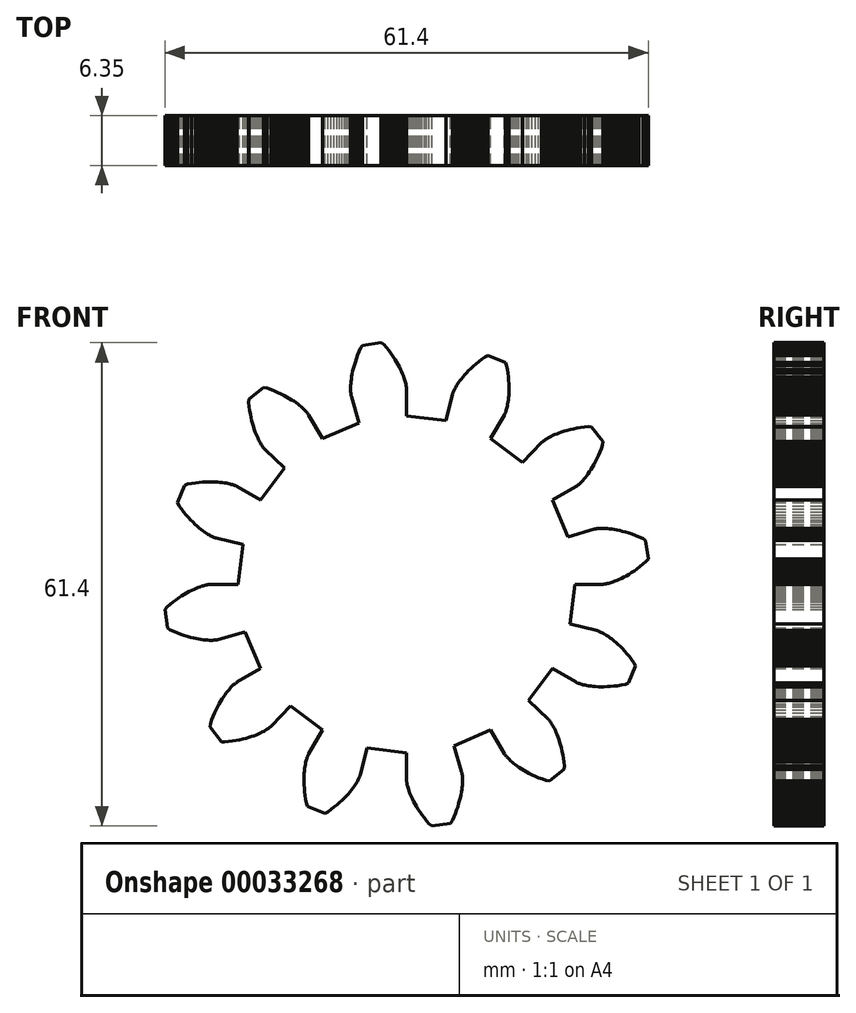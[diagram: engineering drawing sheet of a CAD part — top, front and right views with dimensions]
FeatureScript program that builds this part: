
annotation { "Feature Type Name" : "Feature", "Feature Type Description" : "" }
export const myFeature = defineFeature(function(context is Context, id is Id, definition is map)
    precondition{}
    {
        {
            var Q0;
            Q0=qCreatedBy(makeId("Front.planeOp"),FACE);
            var sketch = newSketch(context, id + "F0", { "sketchPlane" : qUnion([Q0])});
            skLineSegment(sketch, "E0", {"start": v(21.39, 0) * mm, "end": v(24.87, 0) * mm});
            skLineSegment(sketch, "E1", {"start": v(24.87, 0) * mm, "end": v(24.9, 0) * mm});
            skLineSegment(sketch, "E2", {"start": v(24.9, 0) * mm, "end": v(24.93, 0) * mm});
            skLineSegment(sketch, "E3", {"start": v(24.93, 0) * mm, "end": v(25, 0) * mm});
            skLineSegment(sketch, "E4", {"start": v(25, 0) * mm, "end": v(25.08, 0.02) * mm});
            skLineSegment(sketch, "E5", {"start": v(25.08, 0.02) * mm, "end": v(25.2, 0.04) * mm});
            skLineSegment(sketch, "E6", {"start": v(25.2, 0.04) * mm, "end": v(25.32, 0.06) * mm});
            skLineSegment(sketch, "E7", {"start": v(25.32, 0.06) * mm, "end": v(25.46, 0.09) * mm});
            skLineSegment(sketch, "E8", {"start": v(25.46, 0.09) * mm, "end": v(25.63, 0.13) * mm});
            skLineSegment(sketch, "E9", {"start": v(25.63, 0.13) * mm, "end": v(25.81, 0.18) * mm});
            skLineSegment(sketch, "E10", {"start": v(25.81, 0.18) * mm, "end": v(26.02, 0.24) * mm});
            skLineSegment(sketch, "E11", {"start": v(26.02, 0.24) * mm, "end": v(26.24, 0.31) * mm});
            skLineSegment(sketch, "E12", {"start": v(26.24, 0.31) * mm, "end": v(26.48, 0.4) * mm});
            skLineSegment(sketch, "E13", {"start": v(26.48, 0.4) * mm, "end": v(26.73, 0.5) * mm});
            skLineSegment(sketch, "E14", {"start": v(26.73, 0.5) * mm, "end": v(27, 0.62) * mm});
            skLineSegment(sketch, "E15", {"start": v(27, 0.62) * mm, "end": v(27.3, 0.76) * mm});
            skLineSegment(sketch, "E16", {"start": v(27.3, 0.76) * mm, "end": v(27.6, 0.91) * mm});
            skLineSegment(sketch, "E17", {"start": v(27.6, 0.91) * mm, "end": v(27.91, 1.08) * mm});
            skLineSegment(sketch, "E18", {"start": v(27.91, 1.08) * mm, "end": v(28.24, 1.27) * mm});
            skLineSegment(sketch, "E19", {"start": v(28.24, 1.27) * mm, "end": v(28.58, 1.49) * mm});
            skLineSegment(sketch, "E20", {"start": v(28.58, 1.49) * mm, "end": v(28.93, 1.72) * mm});
            skLineSegment(sketch, "E21", {"start": v(28.93, 1.72) * mm, "end": v(29.3, 1.98) * mm});
            skLineSegment(sketch, "E22", {"start": v(29.3, 1.98) * mm, "end": v(29.67, 2.25) * mm});
            skLineSegment(sketch, "E23", {"start": v(29.67, 2.25) * mm, "end": v(30.05, 2.56) * mm});
            skLineSegment(sketch, "E24", {"start": v(30.05, 2.56) * mm, "end": v(30.44, 2.88) * mm});
            skLineSegment(sketch, "E25", {"start": v(30.44, 2.88) * mm, "end": v(30.7, 3.22) * mm});
            skLineSegment(sketch, "E26", {"start": v(30.7, 3.22) * mm, "end": v(30.36, 5.56) * mm});
            skLineSegment(sketch, "E27", {"start": v(30.36, 5.56) * mm, "end": v(30.02, 5.81) * mm});
            skLineSegment(sketch, "E28", {"start": v(30.02, 5.81) * mm, "end": v(29.55, 6.02) * mm});
            skLineSegment(sketch, "E29", {"start": v(29.55, 6.02) * mm, "end": v(29.1, 6.2) * mm});
            skLineSegment(sketch, "E30", {"start": v(29.1, 6.2) * mm, "end": v(28.66, 6.36) * mm});
            skLineSegment(sketch, "E31", {"start": v(28.66, 6.36) * mm, "end": v(28.25, 6.5) * mm});
            skLineSegment(sketch, "E32", {"start": v(28.25, 6.5) * mm, "end": v(27.84, 6.63) * mm});
            skLineSegment(sketch, "E33", {"start": v(27.84, 6.63) * mm, "end": v(27.45, 6.74) * mm});
            skLineSegment(sketch, "E34", {"start": v(27.45, 6.74) * mm, "end": v(27.08, 6.83) * mm});
            skLineSegment(sketch, "E35", {"start": v(27.08, 6.83) * mm, "end": v(26.73, 6.9) * mm});
            skLineSegment(sketch, "E36", {"start": v(26.73, 6.9) * mm, "end": v(26.4, 6.97) * mm});
            skLineSegment(sketch, "E37", {"start": v(26.4, 6.97) * mm, "end": v(26.08, 7.02) * mm});
            skLineSegment(sketch, "E38", {"start": v(26.08, 7.02) * mm, "end": v(25.8, 7.05) * mm});
            skLineSegment(sketch, "E39", {"start": v(25.8, 7.05) * mm, "end": v(25.52, 7.08) * mm});
            skLineSegment(sketch, "E40", {"start": v(25.52, 7.08) * mm, "end": v(25.26, 7.1) * mm});
            skLineSegment(sketch, "E41", {"start": v(25.26, 7.1) * mm, "end": v(25.03, 7.1) * mm});
            skLineSegment(sketch, "E42", {"start": v(25.03, 7.1) * mm, "end": v(24.82, 7.1) * mm});
            skLineSegment(sketch, "E43", {"start": v(24.82, 7.1) * mm, "end": v(24.63, 7.1) * mm});
            skLineSegment(sketch, "E44", {"start": v(24.63, 7.1) * mm, "end": v(24.45, 7.1) * mm});
            skLineSegment(sketch, "E45", {"start": v(24.45, 7.1) * mm, "end": v(24.3, 7.08) * mm});
            skLineSegment(sketch, "E46", {"start": v(24.3, 7.08) * mm, "end": v(24.18, 7.07) * mm});
            skLineSegment(sketch, "E47", {"start": v(24.18, 7.07) * mm, "end": v(24.07, 7.05) * mm});
            skLineSegment(sketch, "E48", {"start": v(24.07, 7.05) * mm, "end": v(23.99, 7.04) * mm});
            skLineSegment(sketch, "E49", {"start": v(23.99, 7.04) * mm, "end": v(23.92, 7.03) * mm});
            skLineSegment(sketch, "E50", {"start": v(23.92, 7.03) * mm, "end": v(23.88, 7.02) * mm});
            skLineSegment(sketch, "E51", {"start": v(23.88, 7.02) * mm, "end": v(23.86, 7.01) * mm});
            skLineSegment(sketch, "E52", {"start": v(23.86, 7.01) * mm, "end": v(20.52, 6.03) * mm});
            skLineSegment(sketch, "E53", {"start": v(20.52, 6.03) * mm, "end": v(18.52, 10.7) * mm});
            skLineSegment(sketch, "E54", {"start": v(18.52, 10.7) * mm, "end": v(21.53, 12.43) * mm});
            skLineSegment(sketch, "E55", {"start": v(21.53, 12.43) * mm, "end": v(21.56, 12.45) * mm});
            skLineSegment(sketch, "E56", {"start": v(21.56, 12.45) * mm, "end": v(21.64, 12.5) * mm});
            skLineSegment(sketch, "E57", {"start": v(21.64, 12.5) * mm, "end": v(21.71, 12.56) * mm});
            skLineSegment(sketch, "E58", {"start": v(21.71, 12.56) * mm, "end": v(21.8, 12.63) * mm});
            skLineSegment(sketch, "E59", {"start": v(21.8, 12.63) * mm, "end": v(21.9, 12.7) * mm});
            skLineSegment(sketch, "E60", {"start": v(21.9, 12.7) * mm, "end": v(22, 12.8) * mm});
            skLineSegment(sketch, "E61", {"start": v(22, 12.8) * mm, "end": v(22.13, 12.93) * mm});
            skLineSegment(sketch, "E62", {"start": v(22.13, 12.93) * mm, "end": v(22.26, 13.06) * mm});
            skLineSegment(sketch, "E63", {"start": v(22.26, 13.06) * mm, "end": v(22.41, 13.22) * mm});
            skLineSegment(sketch, "E64", {"start": v(22.41, 13.22) * mm, "end": v(22.57, 13.4) * mm});
            skLineSegment(sketch, "E65", {"start": v(22.57, 13.4) * mm, "end": v(22.73, 13.59) * mm});
            skLineSegment(sketch, "E66", {"start": v(22.73, 13.59) * mm, "end": v(22.9, 13.8) * mm});
            skLineSegment(sketch, "E67", {"start": v(22.9, 13.8) * mm, "end": v(23.08, 14.04) * mm});
            skLineSegment(sketch, "E68", {"start": v(23.08, 14.04) * mm, "end": v(23.26, 14.3) * mm});
            skLineSegment(sketch, "E69", {"start": v(23.26, 14.3) * mm, "end": v(23.44, 14.59) * mm});
            skLineSegment(sketch, "E70", {"start": v(23.44, 14.59) * mm, "end": v(23.63, 14.9) * mm});
            skLineSegment(sketch, "E71", {"start": v(23.63, 14.9) * mm, "end": v(23.82, 15.22) * mm});
            skLineSegment(sketch, "E72", {"start": v(23.82, 15.22) * mm, "end": v(24, 15.58) * mm});
            skLineSegment(sketch, "E73", {"start": v(24, 15.58) * mm, "end": v(24.2, 15.96) * mm});
            skLineSegment(sketch, "E74", {"start": v(24.2, 15.96) * mm, "end": v(24.38, 16.36) * mm});
            skLineSegment(sketch, "E75", {"start": v(24.38, 16.36) * mm, "end": v(24.57, 16.79) * mm});
            skLineSegment(sketch, "E76", {"start": v(24.57, 16.79) * mm, "end": v(24.74, 17.24) * mm});
            skLineSegment(sketch, "E77", {"start": v(24.74, 17.24) * mm, "end": v(24.92, 17.72) * mm});
            skLineSegment(sketch, "E78", {"start": v(24.92, 17.72) * mm, "end": v(24.98, 18.14) * mm});
            skLineSegment(sketch, "E79", {"start": v(24.98, 18.14) * mm, "end": v(23.51, 20) * mm});
            skLineSegment(sketch, "E80", {"start": v(23.51, 20) * mm, "end": v(23.09, 20.04) * mm});
            skLineSegment(sketch, "E81", {"start": v(23.09, 20.04) * mm, "end": v(22.58, 19.99) * mm});
            skLineSegment(sketch, "E82", {"start": v(22.58, 19.99) * mm, "end": v(22.1, 19.92) * mm});
            skLineSegment(sketch, "E83", {"start": v(22.1, 19.92) * mm, "end": v(21.64, 19.84) * mm});
            skLineSegment(sketch, "E84", {"start": v(21.64, 19.84) * mm, "end": v(21.2, 19.76) * mm});
            skLineSegment(sketch, "E85", {"start": v(21.2, 19.76) * mm, "end": v(20.8, 19.66) * mm});
            skLineSegment(sketch, "E86", {"start": v(20.8, 19.66) * mm, "end": v(20.4, 19.56) * mm});
            skLineSegment(sketch, "E87", {"start": v(20.4, 19.56) * mm, "end": v(20.04, 19.46) * mm});
            skLineSegment(sketch, "E88", {"start": v(20.04, 19.46) * mm, "end": v(19.7, 19.35) * mm});
            skLineSegment(sketch, "E89", {"start": v(19.7, 19.35) * mm, "end": v(19.38, 19.23) * mm});
            skLineSegment(sketch, "E90", {"start": v(19.38, 19.23) * mm, "end": v(19.08, 19.12) * mm});
            skLineSegment(sketch, "E91", {"start": v(19.08, 19.12) * mm, "end": v(18.81, 19) * mm});
            skLineSegment(sketch, "E92", {"start": v(18.81, 19) * mm, "end": v(18.56, 18.89) * mm});
            skLineSegment(sketch, "E93", {"start": v(18.56, 18.89) * mm, "end": v(18.33, 18.78) * mm});
            skLineSegment(sketch, "E94", {"start": v(18.33, 18.78) * mm, "end": v(18.12, 18.67) * mm});
            skLineSegment(sketch, "E95", {"start": v(18.12, 18.67) * mm, "end": v(17.94, 18.56) * mm});
            skLineSegment(sketch, "E96", {"start": v(17.94, 18.56) * mm, "end": v(17.78, 18.46) * mm});
            skLineSegment(sketch, "E97", {"start": v(17.78, 18.46) * mm, "end": v(17.63, 18.37) * mm});
            skLineSegment(sketch, "E98", {"start": v(17.63, 18.37) * mm, "end": v(17.5, 18.29) * mm});
            skLineSegment(sketch, "E99", {"start": v(17.5, 18.29) * mm, "end": v(17.4, 18.2) * mm});
            skLineSegment(sketch, "E100", {"start": v(17.4, 18.2) * mm, "end": v(17.32, 18.14) * mm});
            skLineSegment(sketch, "E101", {"start": v(17.32, 18.14) * mm, "end": v(17.25, 18.09) * mm});
            skLineSegment(sketch, "E102", {"start": v(17.25, 18.09) * mm, "end": v(17.2, 18.05) * mm});
            skLineSegment(sketch, "E103", {"start": v(17.2, 18.05) * mm, "end": v(17.17, 18.02) * mm});
            skLineSegment(sketch, "E104", {"start": v(17.17, 18.02) * mm, "end": v(17.16, 18) * mm});
            skLineSegment(sketch, "E105", {"start": v(17.16, 18) * mm, "end": v(14.76, 15.48) * mm});
            skLineSegment(sketch, "E106", {"start": v(14.76, 15.48) * mm, "end": v(10.7, 18.52) * mm});
            skLineSegment(sketch, "E107", {"start": v(10.7, 18.52) * mm, "end": v(12.43, 21.53) * mm});
            skLineSegment(sketch, "E108", {"start": v(12.43, 21.53) * mm, "end": v(12.44, 21.56) * mm});
            skLineSegment(sketch, "E109", {"start": v(12.44, 21.56) * mm, "end": v(12.46, 21.6) * mm});
            skLineSegment(sketch, "E110", {"start": v(12.46, 21.6) * mm, "end": v(12.5, 21.65) * mm});
            skLineSegment(sketch, "E111", {"start": v(12.5, 21.65) * mm, "end": v(12.53, 21.73) * mm});
            skLineSegment(sketch, "E112", {"start": v(12.53, 21.73) * mm, "end": v(12.56, 21.83) * mm});
            skLineSegment(sketch, "E113", {"start": v(12.56, 21.83) * mm, "end": v(12.6, 21.95) * mm});
            skLineSegment(sketch, "E114", {"start": v(12.6, 21.95) * mm, "end": v(12.65, 22.1) * mm});
            skLineSegment(sketch, "E115", {"start": v(12.65, 22.1) * mm, "end": v(12.7, 22.26) * mm});
            skLineSegment(sketch, "E116", {"start": v(12.7, 22.26) * mm, "end": v(12.75, 22.44) * mm});
            skLineSegment(sketch, "E117", {"start": v(12.75, 22.44) * mm, "end": v(12.8, 22.65) * mm});
            skLineSegment(sketch, "E118", {"start": v(12.8, 22.65) * mm, "end": v(12.85, 22.88) * mm});
            skLineSegment(sketch, "E119", {"start": v(12.85, 22.88) * mm, "end": v(12.9, 23.13) * mm});
            skLineSegment(sketch, "E120", {"start": v(12.9, 23.13) * mm, "end": v(12.93, 23.4) * mm});
            skLineSegment(sketch, "E121", {"start": v(12.93, 23.4) * mm, "end": v(12.96, 23.7) * mm});
            skLineSegment(sketch, "E122", {"start": v(12.96, 23.7) * mm, "end": v(12.99, 24.02) * mm});
            skLineSegment(sketch, "E123", {"start": v(12.99, 24.02) * mm, "end": v(13, 24.35) * mm});
            skLineSegment(sketch, "E124", {"start": v(13, 24.35) * mm, "end": v(13.02, 24.71) * mm});
            skLineSegment(sketch, "E125", {"start": v(13.02, 24.71) * mm, "end": v(13.02, 25.1) * mm});
            skLineSegment(sketch, "E126", {"start": v(13.02, 25.1) * mm, "end": v(13, 25.5) * mm});
            skLineSegment(sketch, "E127", {"start": v(13, 25.5) * mm, "end": v(12.98, 25.92) * mm});
            skLineSegment(sketch, "E128", {"start": v(12.98, 25.92) * mm, "end": v(12.94, 26.36) * mm});
            skLineSegment(sketch, "E129", {"start": v(12.94, 26.36) * mm, "end": v(12.88, 26.82) * mm});
            skLineSegment(sketch, "E130", {"start": v(12.88, 26.82) * mm, "end": v(12.81, 27.3) * mm});
            skLineSegment(sketch, "E131", {"start": v(12.81, 27.3) * mm, "end": v(12.72, 27.8) * mm});
            skLineSegment(sketch, "E132", {"start": v(12.72, 27.8) * mm, "end": v(12.56, 28.2) * mm});
            skLineSegment(sketch, "E133", {"start": v(12.56, 28.2) * mm, "end": v(10.36, 29.08) * mm});
            skLineSegment(sketch, "E134", {"start": v(10.36, 29.08) * mm, "end": v(9.97, 28.9) * mm});
            skLineSegment(sketch, "E135", {"start": v(9.97, 28.9) * mm, "end": v(9.56, 28.6) * mm});
            skLineSegment(sketch, "E136", {"start": v(9.56, 28.6) * mm, "end": v(9.18, 28.3) * mm});
            skLineSegment(sketch, "E137", {"start": v(9.18, 28.3) * mm, "end": v(8.82, 28) * mm});
            skLineSegment(sketch, "E138", {"start": v(8.82, 28) * mm, "end": v(8.49, 27.71) * mm});
            skLineSegment(sketch, "E139", {"start": v(8.49, 27.71) * mm, "end": v(8.18, 27.43) * mm});
            skLineSegment(sketch, "E140", {"start": v(8.18, 27.43) * mm, "end": v(7.9, 27.14) * mm});
            skLineSegment(sketch, "E141", {"start": v(7.9, 27.14) * mm, "end": v(7.63, 26.87) * mm});
            skLineSegment(sketch, "E142", {"start": v(7.63, 26.87) * mm, "end": v(7.39, 26.6) * mm});
            skLineSegment(sketch, "E143", {"start": v(7.39, 26.6) * mm, "end": v(7.17, 26.35) * mm});
            skLineSegment(sketch, "E144", {"start": v(7.17, 26.35) * mm, "end": v(6.97, 26.1) * mm});
            skLineSegment(sketch, "E145", {"start": v(6.97, 26.1) * mm, "end": v(6.79, 25.86) * mm});
            skLineSegment(sketch, "E146", {"start": v(6.79, 25.86) * mm, "end": v(6.63, 25.64) * mm});
            skLineSegment(sketch, "E147", {"start": v(6.63, 25.64) * mm, "end": v(6.49, 25.43) * mm});
            skLineSegment(sketch, "E148", {"start": v(6.49, 25.43) * mm, "end": v(6.36, 25.23) * mm});
            skLineSegment(sketch, "E149", {"start": v(6.36, 25.23) * mm, "end": v(6.25, 25.04) * mm});
            skLineSegment(sketch, "E150", {"start": v(6.25, 25.04) * mm, "end": v(6.16, 24.88) * mm});
            skLineSegment(sketch, "E151", {"start": v(6.16, 24.88) * mm, "end": v(6.09, 24.72) * mm});
            skLineSegment(sketch, "E152", {"start": v(6.09, 24.72) * mm, "end": v(6.02, 24.6) * mm});
            skLineSegment(sketch, "E153", {"start": v(6.02, 24.6) * mm, "end": v(5.97, 24.47) * mm});
            skLineSegment(sketch, "E154", {"start": v(5.97, 24.47) * mm, "end": v(5.93, 24.37) * mm});
            skLineSegment(sketch, "E155", {"start": v(5.93, 24.37) * mm, "end": v(5.9, 24.3) * mm});
            skLineSegment(sketch, "E156", {"start": v(5.9, 24.3) * mm, "end": v(5.88, 24.23) * mm});
            skLineSegment(sketch, "E157", {"start": v(5.88, 24.23) * mm, "end": v(5.86, 24.19) * mm});
            skLineSegment(sketch, "E158", {"start": v(5.86, 24.19) * mm, "end": v(5.86, 24.17) * mm});
            skLineSegment(sketch, "E159", {"start": v(5.86, 24.17) * mm, "end": v(5.04, 20.79) * mm});
            skLineSegment(sketch, "E160", {"start": v(5.04, 20.79) * mm, "end": v(0, 21.39) * mm});
            skLineSegment(sketch, "E161", {"start": v(0, 21.39) * mm, "end": v(0, 24.87) * mm});
            skLineSegment(sketch, "E162", {"start": v(0, 24.87) * mm, "end": v(0, 24.9) * mm});
            skLineSegment(sketch, "E163", {"start": v(0, 24.9) * mm, "end": v(0, 24.93) * mm});
            skLineSegment(sketch, "E164", {"start": v(0, 24.93) * mm, "end": v(0, 25) * mm});
            skLineSegment(sketch, "E165", {"start": v(0, 25) * mm, "end": v(-0.02, 25.08) * mm});
            skLineSegment(sketch, "E166", {"start": v(-0.02, 25.08) * mm, "end": v(-0.04, 25.2) * mm});
            skLineSegment(sketch, "E167", {"start": v(-0.04, 25.2) * mm, "end": v(-0.06, 25.32) * mm});
            skLineSegment(sketch, "E168", {"start": v(-0.06, 25.32) * mm, "end": v(-0.09, 25.46) * mm});
            skLineSegment(sketch, "E169", {"start": v(-0.09, 25.46) * mm, "end": v(-0.13, 25.63) * mm});
            skLineSegment(sketch, "E170", {"start": v(-0.13, 25.63) * mm, "end": v(-0.18, 25.81) * mm});
            skLineSegment(sketch, "E171", {"start": v(-0.18, 25.81) * mm, "end": v(-0.24, 26.02) * mm});
            skLineSegment(sketch, "E172", {"start": v(-0.24, 26.02) * mm, "end": v(-0.31, 26.24) * mm});
            skLineSegment(sketch, "E173", {"start": v(-0.31, 26.24) * mm, "end": v(-0.4, 26.48) * mm});
            skLineSegment(sketch, "E174", {"start": v(-0.4, 26.48) * mm, "end": v(-0.5, 26.73) * mm});
            skLineSegment(sketch, "E175", {"start": v(-0.5, 26.73) * mm, "end": v(-0.62, 27) * mm});
            skLineSegment(sketch, "E176", {"start": v(-0.62, 27) * mm, "end": v(-0.76, 27.3) * mm});
            skLineSegment(sketch, "E177", {"start": v(-0.76, 27.3) * mm, "end": v(-0.91, 27.6) * mm});
            skLineSegment(sketch, "E178", {"start": v(-0.91, 27.6) * mm, "end": v(-1.08, 27.91) * mm});
            skLineSegment(sketch, "E179", {"start": v(-1.08, 27.91) * mm, "end": v(-1.27, 28.24) * mm});
            skLineSegment(sketch, "E180", {"start": v(-1.27, 28.24) * mm, "end": v(-1.49, 28.58) * mm});
            skLineSegment(sketch, "E181", {"start": v(-1.49, 28.58) * mm, "end": v(-1.72, 28.93) * mm});
            skLineSegment(sketch, "E182", {"start": v(-1.72, 28.93) * mm, "end": v(-1.98, 29.3) * mm});
            skLineSegment(sketch, "E183", {"start": v(-1.98, 29.3) * mm, "end": v(-2.25, 29.67) * mm});
            skLineSegment(sketch, "E184", {"start": v(-2.25, 29.67) * mm, "end": v(-2.56, 30.05) * mm});
            skLineSegment(sketch, "E185", {"start": v(-2.56, 30.05) * mm, "end": v(-2.88, 30.44) * mm});
            skLineSegment(sketch, "E186", {"start": v(-2.88, 30.44) * mm, "end": v(-3.22, 30.7) * mm});
            skLineSegment(sketch, "E187", {"start": v(-3.22, 30.7) * mm, "end": v(-5.56, 30.36) * mm});
            skLineSegment(sketch, "E188", {"start": v(-5.56, 30.36) * mm, "end": v(-5.81, 30.02) * mm});
            skLineSegment(sketch, "E189", {"start": v(-5.81, 30.02) * mm, "end": v(-6.02, 29.55) * mm});
            skLineSegment(sketch, "E190", {"start": v(-6.02, 29.55) * mm, "end": v(-6.2, 29.1) * mm});
            skLineSegment(sketch, "E191", {"start": v(-6.2, 29.1) * mm, "end": v(-6.36, 28.66) * mm});
            skLineSegment(sketch, "E192", {"start": v(-6.36, 28.66) * mm, "end": v(-6.5, 28.25) * mm});
            skLineSegment(sketch, "E193", {"start": v(-6.5, 28.25) * mm, "end": v(-6.63, 27.84) * mm});
            skLineSegment(sketch, "E194", {"start": v(-6.63, 27.84) * mm, "end": v(-6.74, 27.45) * mm});
            skLineSegment(sketch, "E195", {"start": v(-6.74, 27.45) * mm, "end": v(-6.83, 27.08) * mm});
            skLineSegment(sketch, "E196", {"start": v(-6.83, 27.08) * mm, "end": v(-6.9, 26.73) * mm});
            skLineSegment(sketch, "E197", {"start": v(-6.9, 26.73) * mm, "end": v(-6.97, 26.4) * mm});
            skLineSegment(sketch, "E198", {"start": v(-6.97, 26.4) * mm, "end": v(-7.02, 26.08) * mm});
            skLineSegment(sketch, "E199", {"start": v(-7.02, 26.08) * mm, "end": v(-7.05, 25.8) * mm});
            skLineSegment(sketch, "E200", {"start": v(-7.05, 25.8) * mm, "end": v(-7.08, 25.52) * mm});
            skLineSegment(sketch, "E201", {"start": v(-7.08, 25.52) * mm, "end": v(-7.1, 25.26) * mm});
            skLineSegment(sketch, "E202", {"start": v(-7.1, 25.26) * mm, "end": v(-7.1, 25.03) * mm});
            skLineSegment(sketch, "E203", {"start": v(-7.1, 25.03) * mm, "end": v(-7.1, 24.82) * mm});
            skLineSegment(sketch, "E204", {"start": v(-7.1, 24.82) * mm, "end": v(-7.1, 24.63) * mm});
            skLineSegment(sketch, "E205", {"start": v(-7.1, 24.63) * mm, "end": v(-7.1, 24.45) * mm});
            skLineSegment(sketch, "E206", {"start": v(-7.1, 24.45) * mm, "end": v(-7.08, 24.3) * mm});
            skLineSegment(sketch, "E207", {"start": v(-7.08, 24.3) * mm, "end": v(-7.07, 24.18) * mm});
            skLineSegment(sketch, "E208", {"start": v(-7.07, 24.18) * mm, "end": v(-7.05, 24.07) * mm});
            skLineSegment(sketch, "E209", {"start": v(-7.05, 24.07) * mm, "end": v(-7.04, 23.99) * mm});
            skLineSegment(sketch, "E210", {"start": v(-7.04, 23.99) * mm, "end": v(-7.03, 23.92) * mm});
            skLineSegment(sketch, "E211", {"start": v(-7.03, 23.92) * mm, "end": v(-7.02, 23.88) * mm});
            skLineSegment(sketch, "E212", {"start": v(-7.02, 23.88) * mm, "end": v(-7, 23.86) * mm});
            skLineSegment(sketch, "E213", {"start": v(-7, 23.86) * mm, "end": v(-6.03, 20.52) * mm});
            skLineSegment(sketch, "E214", {"start": v(-6.03, 20.52) * mm, "end": v(-10.7, 18.52) * mm});
            skLineSegment(sketch, "E215", {"start": v(-10.7, 18.52) * mm, "end": v(-12.43, 21.53) * mm});
            skLineSegment(sketch, "E216", {"start": v(-12.43, 21.53) * mm, "end": v(-12.44, 21.56) * mm});
            skLineSegment(sketch, "E217", {"start": v(-12.44, 21.56) * mm, "end": v(-12.5, 21.64) * mm});
            skLineSegment(sketch, "E218", {"start": v(-12.5, 21.64) * mm, "end": v(-12.56, 21.71) * mm});
            skLineSegment(sketch, "E219", {"start": v(-12.56, 21.71) * mm, "end": v(-12.63, 21.8) * mm});
            skLineSegment(sketch, "E220", {"start": v(-12.63, 21.8) * mm, "end": v(-12.7, 21.9) * mm});
            skLineSegment(sketch, "E221", {"start": v(-12.7, 21.9) * mm, "end": v(-12.8, 22) * mm});
            skLineSegment(sketch, "E222", {"start": v(-12.8, 22) * mm, "end": v(-12.93, 22.13) * mm});
            skLineSegment(sketch, "E223", {"start": v(-12.93, 22.13) * mm, "end": v(-13.06, 22.26) * mm});
            skLineSegment(sketch, "E224", {"start": v(-13.06, 22.26) * mm, "end": v(-13.22, 22.41) * mm});
            skLineSegment(sketch, "E225", {"start": v(-13.22, 22.41) * mm, "end": v(-13.4, 22.57) * mm});
            skLineSegment(sketch, "E226", {"start": v(-13.4, 22.57) * mm, "end": v(-13.59, 22.73) * mm});
            skLineSegment(sketch, "E227", {"start": v(-13.59, 22.73) * mm, "end": v(-13.8, 22.9) * mm});
            skLineSegment(sketch, "E228", {"start": v(-13.8, 22.9) * mm, "end": v(-14.04, 23.08) * mm});
            skLineSegment(sketch, "E229", {"start": v(-14.04, 23.08) * mm, "end": v(-14.3, 23.26) * mm});
            skLineSegment(sketch, "E230", {"start": v(-14.3, 23.26) * mm, "end": v(-14.59, 23.44) * mm});
            skLineSegment(sketch, "E231", {"start": v(-14.59, 23.44) * mm, "end": v(-14.9, 23.63) * mm});
            skLineSegment(sketch, "E232", {"start": v(-14.9, 23.63) * mm, "end": v(-15.22, 23.82) * mm});
            skLineSegment(sketch, "E233", {"start": v(-15.22, 23.82) * mm, "end": v(-15.58, 24) * mm});
            skLineSegment(sketch, "E234", {"start": v(-15.58, 24) * mm, "end": v(-15.96, 24.2) * mm});
            skLineSegment(sketch, "E235", {"start": v(-15.96, 24.2) * mm, "end": v(-16.36, 24.38) * mm});
            skLineSegment(sketch, "E236", {"start": v(-16.36, 24.38) * mm, "end": v(-16.79, 24.57) * mm});
            skLineSegment(sketch, "E237", {"start": v(-16.79, 24.57) * mm, "end": v(-17.24, 24.74) * mm});
            skLineSegment(sketch, "E238", {"start": v(-17.24, 24.74) * mm, "end": v(-17.72, 24.92) * mm});
            skLineSegment(sketch, "E239", {"start": v(-17.72, 24.92) * mm, "end": v(-18.14, 24.98) * mm});
            skLineSegment(sketch, "E240", {"start": v(-18.14, 24.98) * mm, "end": v(-20, 23.51) * mm});
            skLineSegment(sketch, "E241", {"start": v(-20, 23.51) * mm, "end": v(-20.04, 23.09) * mm});
            skLineSegment(sketch, "E242", {"start": v(-20.04, 23.09) * mm, "end": v(-19.99, 22.58) * mm});
            skLineSegment(sketch, "E243", {"start": v(-19.99, 22.58) * mm, "end": v(-19.92, 22.1) * mm});
            skLineSegment(sketch, "E244", {"start": v(-19.92, 22.1) * mm, "end": v(-19.84, 21.64) * mm});
            skLineSegment(sketch, "E245", {"start": v(-19.84, 21.64) * mm, "end": v(-19.76, 21.2) * mm});
            skLineSegment(sketch, "E246", {"start": v(-19.76, 21.2) * mm, "end": v(-19.66, 20.8) * mm});
            skLineSegment(sketch, "E247", {"start": v(-19.66, 20.8) * mm, "end": v(-19.56, 20.4) * mm});
            skLineSegment(sketch, "E248", {"start": v(-19.56, 20.4) * mm, "end": v(-19.46, 20.04) * mm});
            skLineSegment(sketch, "E249", {"start": v(-19.46, 20.04) * mm, "end": v(-19.35, 19.7) * mm});
            skLineSegment(sketch, "E250", {"start": v(-19.35, 19.7) * mm, "end": v(-19.23, 19.38) * mm});
            skLineSegment(sketch, "E251", {"start": v(-19.23, 19.38) * mm, "end": v(-19.12, 19.08) * mm});
            skLineSegment(sketch, "E252", {"start": v(-19.12, 19.08) * mm, "end": v(-19, 18.81) * mm});
            skLineSegment(sketch, "E253", {"start": v(-19, 18.81) * mm, "end": v(-18.89, 18.56) * mm});
            skLineSegment(sketch, "E254", {"start": v(-18.89, 18.56) * mm, "end": v(-18.78, 18.33) * mm});
            skLineSegment(sketch, "E255", {"start": v(-18.78, 18.33) * mm, "end": v(-18.67, 18.12) * mm});
            skLineSegment(sketch, "E256", {"start": v(-18.67, 18.12) * mm, "end": v(-18.56, 17.94) * mm});
            skLineSegment(sketch, "E257", {"start": v(-18.56, 17.94) * mm, "end": v(-18.46, 17.78) * mm});
            skLineSegment(sketch, "E258", {"start": v(-18.46, 17.78) * mm, "end": v(-18.37, 17.63) * mm});
            skLineSegment(sketch, "E259", {"start": v(-18.37, 17.63) * mm, "end": v(-18.29, 17.5) * mm});
            skLineSegment(sketch, "E260", {"start": v(-18.29, 17.5) * mm, "end": v(-18.2, 17.4) * mm});
            skLineSegment(sketch, "E261", {"start": v(-18.2, 17.4) * mm, "end": v(-18.14, 17.32) * mm});
            skLineSegment(sketch, "E262", {"start": v(-18.14, 17.32) * mm, "end": v(-18.09, 17.25) * mm});
            skLineSegment(sketch, "E263", {"start": v(-18.09, 17.25) * mm, "end": v(-18.05, 17.2) * mm});
            skLineSegment(sketch, "E264", {"start": v(-18.05, 17.2) * mm, "end": v(-18.02, 17.17) * mm});
            skLineSegment(sketch, "E265", {"start": v(-18.02, 17.17) * mm, "end": v(-18, 17.16) * mm});
            skLineSegment(sketch, "E266", {"start": v(-18, 17.16) * mm, "end": v(-15.48, 14.76) * mm});
            skLineSegment(sketch, "E267", {"start": v(-15.48, 14.76) * mm, "end": v(-18.52, 10.7) * mm});
            skLineSegment(sketch, "E268", {"start": v(-18.52, 10.7) * mm, "end": v(-21.53, 12.43) * mm});
            skLineSegment(sketch, "E269", {"start": v(-21.53, 12.43) * mm, "end": v(-21.56, 12.44) * mm});
            skLineSegment(sketch, "E270", {"start": v(-21.56, 12.44) * mm, "end": v(-21.6, 12.46) * mm});
            skLineSegment(sketch, "E271", {"start": v(-21.6, 12.46) * mm, "end": v(-21.65, 12.5) * mm});
            skLineSegment(sketch, "E272", {"start": v(-21.65, 12.5) * mm, "end": v(-21.73, 12.53) * mm});
            skLineSegment(sketch, "E273", {"start": v(-21.73, 12.53) * mm, "end": v(-21.83, 12.56) * mm});
            skLineSegment(sketch, "E274", {"start": v(-21.83, 12.56) * mm, "end": v(-21.95, 12.6) * mm});
            skLineSegment(sketch, "E275", {"start": v(-21.95, 12.6) * mm, "end": v(-22.1, 12.65) * mm});
            skLineSegment(sketch, "E276", {"start": v(-22.1, 12.65) * mm, "end": v(-22.26, 12.7) * mm});
            skLineSegment(sketch, "E277", {"start": v(-22.26, 12.7) * mm, "end": v(-22.44, 12.75) * mm});
            skLineSegment(sketch, "E278", {"start": v(-22.44, 12.75) * mm, "end": v(-22.65, 12.8) * mm});
            skLineSegment(sketch, "E279", {"start": v(-22.65, 12.8) * mm, "end": v(-22.88, 12.85) * mm});
            skLineSegment(sketch, "E280", {"start": v(-22.88, 12.85) * mm, "end": v(-23.13, 12.9) * mm});
            skLineSegment(sketch, "E281", {"start": v(-23.13, 12.9) * mm, "end": v(-23.4, 12.93) * mm});
            skLineSegment(sketch, "E282", {"start": v(-23.4, 12.93) * mm, "end": v(-23.7, 12.96) * mm});
            skLineSegment(sketch, "E283", {"start": v(-23.7, 12.96) * mm, "end": v(-24.01, 12.99) * mm});
            skLineSegment(sketch, "E284", {"start": v(-24.01, 12.99) * mm, "end": v(-24.35, 13) * mm});
            skLineSegment(sketch, "E285", {"start": v(-24.35, 13) * mm, "end": v(-24.71, 13.02) * mm});
            skLineSegment(sketch, "E286", {"start": v(-24.71, 13.02) * mm, "end": v(-25.1, 13.02) * mm});
            skLineSegment(sketch, "E287", {"start": v(-25.1, 13.02) * mm, "end": v(-25.5, 13) * mm});
            skLineSegment(sketch, "E288", {"start": v(-25.5, 13) * mm, "end": v(-25.92, 12.98) * mm});
            skLineSegment(sketch, "E289", {"start": v(-25.92, 12.98) * mm, "end": v(-26.36, 12.94) * mm});
            skLineSegment(sketch, "E290", {"start": v(-26.36, 12.94) * mm, "end": v(-26.82, 12.88) * mm});
            skLineSegment(sketch, "E291", {"start": v(-26.82, 12.88) * mm, "end": v(-27.3, 12.81) * mm});
            skLineSegment(sketch, "E292", {"start": v(-27.3, 12.81) * mm, "end": v(-27.8, 12.72) * mm});
            skLineSegment(sketch, "E293", {"start": v(-27.8, 12.72) * mm, "end": v(-28.2, 12.56) * mm});
            skLineSegment(sketch, "E294", {"start": v(-28.2, 12.56) * mm, "end": v(-29.08, 10.36) * mm});
            skLineSegment(sketch, "E295", {"start": v(-29.08, 10.36) * mm, "end": v(-28.9, 9.97) * mm});
            skLineSegment(sketch, "E296", {"start": v(-28.9, 9.97) * mm, "end": v(-28.6, 9.56) * mm});
            skLineSegment(sketch, "E297", {"start": v(-28.6, 9.56) * mm, "end": v(-28.3, 9.18) * mm});
            skLineSegment(sketch, "E298", {"start": v(-28.3, 9.18) * mm, "end": v(-28, 8.82) * mm});
            skLineSegment(sketch, "E299", {"start": v(-28, 8.82) * mm, "end": v(-27.71, 8.49) * mm});
            skLineSegment(sketch, "E300", {"start": v(-27.71, 8.49) * mm, "end": v(-27.43, 8.18) * mm});
            skLineSegment(sketch, "E301", {"start": v(-27.43, 8.18) * mm, "end": v(-27.14, 7.9) * mm});
            skLineSegment(sketch, "E302", {"start": v(-27.14, 7.9) * mm, "end": v(-26.87, 7.63) * mm});
            skLineSegment(sketch, "E303", {"start": v(-26.87, 7.63) * mm, "end": v(-26.6, 7.39) * mm});
            skLineSegment(sketch, "E304", {"start": v(-26.6, 7.39) * mm, "end": v(-26.35, 7.17) * mm});
            skLineSegment(sketch, "E305", {"start": v(-26.35, 7.17) * mm, "end": v(-26.1, 6.97) * mm});
            skLineSegment(sketch, "E306", {"start": v(-26.1, 6.97) * mm, "end": v(-25.86, 6.79) * mm});
            skLineSegment(sketch, "E307", {"start": v(-25.86, 6.79) * mm, "end": v(-25.64, 6.63) * mm});
            skLineSegment(sketch, "E308", {"start": v(-25.64, 6.63) * mm, "end": v(-25.43, 6.49) * mm});
            skLineSegment(sketch, "E309", {"start": v(-25.43, 6.49) * mm, "end": v(-25.23, 6.36) * mm});
            skLineSegment(sketch, "E310", {"start": v(-25.23, 6.36) * mm, "end": v(-25.04, 6.25) * mm});
            skLineSegment(sketch, "E311", {"start": v(-25.04, 6.25) * mm, "end": v(-24.88, 6.16) * mm});
            skLineSegment(sketch, "E312", {"start": v(-24.88, 6.16) * mm, "end": v(-24.72, 6.09) * mm});
            skLineSegment(sketch, "E313", {"start": v(-24.72, 6.09) * mm, "end": v(-24.6, 6.02) * mm});
            skLineSegment(sketch, "E314", {"start": v(-24.6, 6.02) * mm, "end": v(-24.47, 5.97) * mm});
            skLineSegment(sketch, "E315", {"start": v(-24.47, 5.97) * mm, "end": v(-24.37, 5.93) * mm});
            skLineSegment(sketch, "E316", {"start": v(-24.37, 5.93) * mm, "end": v(-24.3, 5.9) * mm});
            skLineSegment(sketch, "E317", {"start": v(-24.3, 5.9) * mm, "end": v(-24.23, 5.88) * mm});
            skLineSegment(sketch, "E318", {"start": v(-24.23, 5.88) * mm, "end": v(-24.19, 5.86) * mm});
            skLineSegment(sketch, "E319", {"start": v(-24.19, 5.86) * mm, "end": v(-24.17, 5.86) * mm});
            skLineSegment(sketch, "E320", {"start": v(-24.17, 5.86) * mm, "end": v(-20.78, 5.04) * mm});
            skLineSegment(sketch, "E321", {"start": v(-20.78, 5.04) * mm, "end": v(-21.39, 0) * mm});
            skLineSegment(sketch, "E322", {"start": v(-21.39, 0) * mm, "end": v(-24.87, 0) * mm});
            skLineSegment(sketch, "E323", {"start": v(-24.87, 0) * mm, "end": v(-24.9, 0) * mm});
            skLineSegment(sketch, "E324", {"start": v(-24.9, 0) * mm, "end": v(-24.93, 0) * mm});
            skLineSegment(sketch, "E325", {"start": v(-24.93, 0) * mm, "end": v(-25, 0) * mm});
            skLineSegment(sketch, "E326", {"start": v(-25, 0) * mm, "end": v(-25.08, -0.02) * mm});
            skLineSegment(sketch, "E327", {"start": v(-25.08, -0.02) * mm, "end": v(-25.2, -0.04) * mm});
            skLineSegment(sketch, "E328", {"start": v(-25.2, -0.04) * mm, "end": v(-25.32, -0.06) * mm});
            skLineSegment(sketch, "E329", {"start": v(-25.32, -0.06) * mm, "end": v(-25.46, -0.09) * mm});
            skLineSegment(sketch, "E330", {"start": v(-25.46, -0.09) * mm, "end": v(-25.63, -0.13) * mm});
            skLineSegment(sketch, "E331", {"start": v(-25.63, -0.13) * mm, "end": v(-25.81, -0.18) * mm});
            skLineSegment(sketch, "E332", {"start": v(-25.81, -0.18) * mm, "end": v(-26.02, -0.24) * mm});
            skLineSegment(sketch, "E333", {"start": v(-26.02, -0.24) * mm, "end": v(-26.24, -0.31) * mm});
            skLineSegment(sketch, "E334", {"start": v(-26.24, -0.31) * mm, "end": v(-26.48, -0.4) * mm});
            skLineSegment(sketch, "E335", {"start": v(-26.48, -0.4) * mm, "end": v(-26.73, -0.5) * mm});
            skLineSegment(sketch, "E336", {"start": v(-26.73, -0.5) * mm, "end": v(-27, -0.62) * mm});
            skLineSegment(sketch, "E337", {"start": v(-27, -0.62) * mm, "end": v(-27.3, -0.76) * mm});
            skLineSegment(sketch, "E338", {"start": v(-27.3, -0.76) * mm, "end": v(-27.6, -0.91) * mm});
            skLineSegment(sketch, "E339", {"start": v(-27.6, -0.91) * mm, "end": v(-27.91, -1.08) * mm});
            skLineSegment(sketch, "E340", {"start": v(-27.91, -1.08) * mm, "end": v(-28.24, -1.27) * mm});
            skLineSegment(sketch, "E341", {"start": v(-28.24, -1.27) * mm, "end": v(-28.58, -1.49) * mm});
            skLineSegment(sketch, "E342", {"start": v(-28.58, -1.49) * mm, "end": v(-28.93, -1.72) * mm});
            skLineSegment(sketch, "E343", {"start": v(-28.93, -1.72) * mm, "end": v(-29.3, -1.98) * mm});
            skLineSegment(sketch, "E344", {"start": v(-29.3, -1.98) * mm, "end": v(-29.67, -2.25) * mm});
            skLineSegment(sketch, "E345", {"start": v(-29.67, -2.25) * mm, "end": v(-30.05, -2.56) * mm});
            skLineSegment(sketch, "E346", {"start": v(-30.05, -2.56) * mm, "end": v(-30.44, -2.88) * mm});
            skLineSegment(sketch, "E347", {"start": v(-30.44, -2.88) * mm, "end": v(-30.7, -3.22) * mm});
            skLineSegment(sketch, "E348", {"start": v(-30.7, -3.22) * mm, "end": v(-30.36, -5.56) * mm});
            skLineSegment(sketch, "E349", {"start": v(-30.36, -5.56) * mm, "end": v(-30.01, -5.81) * mm});
            skLineSegment(sketch, "E350", {"start": v(-30.01, -5.81) * mm, "end": v(-29.55, -6.02) * mm});
            skLineSegment(sketch, "E351", {"start": v(-29.55, -6.02) * mm, "end": v(-29.1, -6.2) * mm});
            skLineSegment(sketch, "E352", {"start": v(-29.1, -6.2) * mm, "end": v(-28.66, -6.36) * mm});
            skLineSegment(sketch, "E353", {"start": v(-28.66, -6.36) * mm, "end": v(-28.25, -6.5) * mm});
            skLineSegment(sketch, "E354", {"start": v(-28.25, -6.5) * mm, "end": v(-27.84, -6.63) * mm});
            skLineSegment(sketch, "E355", {"start": v(-27.84, -6.63) * mm, "end": v(-27.45, -6.74) * mm});
            skLineSegment(sketch, "E356", {"start": v(-27.45, -6.74) * mm, "end": v(-27.08, -6.83) * mm});
            skLineSegment(sketch, "E357", {"start": v(-27.08, -6.83) * mm, "end": v(-26.73, -6.9) * mm});
            skLineSegment(sketch, "E358", {"start": v(-26.73, -6.9) * mm, "end": v(-26.4, -6.97) * mm});
            skLineSegment(sketch, "E359", {"start": v(-26.4, -6.97) * mm, "end": v(-26.08, -7.02) * mm});
            skLineSegment(sketch, "E360", {"start": v(-26.08, -7.02) * mm, "end": v(-25.8, -7.05) * mm});
            skLineSegment(sketch, "E361", {"start": v(-25.8, -7.05) * mm, "end": v(-25.52, -7.08) * mm});
            skLineSegment(sketch, "E362", {"start": v(-25.52, -7.08) * mm, "end": v(-25.26, -7.1) * mm});
            skLineSegment(sketch, "E363", {"start": v(-25.26, -7.1) * mm, "end": v(-25.03, -7.1) * mm});
            skLineSegment(sketch, "E364", {"start": v(-25.03, -7.1) * mm, "end": v(-24.82, -7.1) * mm});
            skLineSegment(sketch, "E365", {"start": v(-24.82, -7.1) * mm, "end": v(-24.63, -7.1) * mm});
            skLineSegment(sketch, "E366", {"start": v(-24.63, -7.1) * mm, "end": v(-24.45, -7.1) * mm});
            skLineSegment(sketch, "E367", {"start": v(-24.45, -7.1) * mm, "end": v(-24.3, -7.08) * mm});
            skLineSegment(sketch, "E368", {"start": v(-24.3, -7.08) * mm, "end": v(-24.18, -7.07) * mm});
            skLineSegment(sketch, "E369", {"start": v(-24.18, -7.07) * mm, "end": v(-24.07, -7.05) * mm});
            skLineSegment(sketch, "E370", {"start": v(-24.07, -7.05) * mm, "end": v(-23.99, -7.04) * mm});
            skLineSegment(sketch, "E371", {"start": v(-23.99, -7.04) * mm, "end": v(-23.92, -7.03) * mm});
            skLineSegment(sketch, "E372", {"start": v(-23.92, -7.03) * mm, "end": v(-23.88, -7.02) * mm});
            skLineSegment(sketch, "E373", {"start": v(-23.88, -7.02) * mm, "end": v(-23.86, -7) * mm});
            skLineSegment(sketch, "E374", {"start": v(-23.86, -7) * mm, "end": v(-20.52, -6.03) * mm});
            skLineSegment(sketch, "E375", {"start": v(-20.52, -6.03) * mm, "end": v(-18.52, -10.7) * mm});
            skLineSegment(sketch, "E376", {"start": v(-18.52, -10.7) * mm, "end": v(-21.53, -12.43) * mm});
            skLineSegment(sketch, "E377", {"start": v(-21.53, -12.43) * mm, "end": v(-21.56, -12.44) * mm});
            skLineSegment(sketch, "E378", {"start": v(-21.56, -12.44) * mm, "end": v(-21.64, -12.5) * mm});
            skLineSegment(sketch, "E379", {"start": v(-21.64, -12.5) * mm, "end": v(-21.71, -12.56) * mm});
            skLineSegment(sketch, "E380", {"start": v(-21.71, -12.56) * mm, "end": v(-21.8, -12.63) * mm});
            skLineSegment(sketch, "E381", {"start": v(-21.8, -12.63) * mm, "end": v(-21.9, -12.7) * mm});
            skLineSegment(sketch, "E382", {"start": v(-21.9, -12.7) * mm, "end": v(-22, -12.8) * mm});
            skLineSegment(sketch, "E383", {"start": v(-22, -12.8) * mm, "end": v(-22.13, -12.93) * mm});
            skLineSegment(sketch, "E384", {"start": v(-22.13, -12.93) * mm, "end": v(-22.26, -13.06) * mm});
            skLineSegment(sketch, "E385", {"start": v(-22.26, -13.06) * mm, "end": v(-22.41, -13.22) * mm});
            skLineSegment(sketch, "E386", {"start": v(-22.41, -13.22) * mm, "end": v(-22.57, -13.4) * mm});
            skLineSegment(sketch, "E387", {"start": v(-22.57, -13.4) * mm, "end": v(-22.73, -13.59) * mm});
            skLineSegment(sketch, "E388", {"start": v(-22.73, -13.59) * mm, "end": v(-22.9, -13.8) * mm});
            skLineSegment(sketch, "E389", {"start": v(-22.9, -13.8) * mm, "end": v(-23.08, -14.04) * mm});
            skLineSegment(sketch, "E390", {"start": v(-23.08, -14.04) * mm, "end": v(-23.26, -14.3) * mm});
            skLineSegment(sketch, "E391", {"start": v(-23.26, -14.3) * mm, "end": v(-23.44, -14.59) * mm});
            skLineSegment(sketch, "E392", {"start": v(-23.44, -14.59) * mm, "end": v(-23.63, -14.9) * mm});
            skLineSegment(sketch, "E393", {"start": v(-23.63, -14.9) * mm, "end": v(-23.82, -15.22) * mm});
            skLineSegment(sketch, "E394", {"start": v(-23.82, -15.22) * mm, "end": v(-24, -15.58) * mm});
            skLineSegment(sketch, "E395", {"start": v(-24, -15.58) * mm, "end": v(-24.2, -15.96) * mm});
            skLineSegment(sketch, "E396", {"start": v(-24.2, -15.96) * mm, "end": v(-24.38, -16.36) * mm});
            skLineSegment(sketch, "E397", {"start": v(-24.38, -16.36) * mm, "end": v(-24.57, -16.79) * mm});
            skLineSegment(sketch, "E398", {"start": v(-24.57, -16.79) * mm, "end": v(-24.74, -17.24) * mm});
            skLineSegment(sketch, "E399", {"start": v(-24.74, -17.24) * mm, "end": v(-24.92, -17.72) * mm});
            skLineSegment(sketch, "E400", {"start": v(-24.92, -17.72) * mm, "end": v(-24.98, -18.14) * mm});
            skLineSegment(sketch, "E401", {"start": v(-24.98, -18.14) * mm, "end": v(-23.51, -20) * mm});
            skLineSegment(sketch, "E402", {"start": v(-23.51, -20) * mm, "end": v(-23.09, -20.04) * mm});
            skLineSegment(sketch, "E403", {"start": v(-23.09, -20.04) * mm, "end": v(-22.58, -19.99) * mm});
            skLineSegment(sketch, "E404", {"start": v(-22.58, -19.99) * mm, "end": v(-22.1, -19.92) * mm});
            skLineSegment(sketch, "E405", {"start": v(-22.1, -19.92) * mm, "end": v(-21.64, -19.84) * mm});
            skLineSegment(sketch, "E406", {"start": v(-21.64, -19.84) * mm, "end": v(-21.2, -19.76) * mm});
            skLineSegment(sketch, "E407", {"start": v(-21.2, -19.76) * mm, "end": v(-20.8, -19.66) * mm});
            skLineSegment(sketch, "E408", {"start": v(-20.8, -19.66) * mm, "end": v(-20.4, -19.56) * mm});
            skLineSegment(sketch, "E409", {"start": v(-20.4, -19.56) * mm, "end": v(-20.04, -19.46) * mm});
            skLineSegment(sketch, "E410", {"start": v(-20.04, -19.46) * mm, "end": v(-19.7, -19.35) * mm});
            skLineSegment(sketch, "E411", {"start": v(-19.7, -19.35) * mm, "end": v(-19.38, -19.23) * mm});
            skLineSegment(sketch, "E412", {"start": v(-19.38, -19.23) * mm, "end": v(-19.08, -19.12) * mm});
            skLineSegment(sketch, "E413", {"start": v(-19.08, -19.12) * mm, "end": v(-18.81, -19) * mm});
            skLineSegment(sketch, "E414", {"start": v(-18.81, -19) * mm, "end": v(-18.56, -18.89) * mm});
            skLineSegment(sketch, "E415", {"start": v(-18.56, -18.89) * mm, "end": v(-18.33, -18.78) * mm});
            skLineSegment(sketch, "E416", {"start": v(-18.33, -18.78) * mm, "end": v(-18.12, -18.67) * mm});
            skLineSegment(sketch, "E417", {"start": v(-18.12, -18.67) * mm, "end": v(-17.94, -18.56) * mm});
            skLineSegment(sketch, "E418", {"start": v(-17.94, -18.56) * mm, "end": v(-17.78, -18.46) * mm});
            skLineSegment(sketch, "E419", {"start": v(-17.78, -18.46) * mm, "end": v(-17.63, -18.37) * mm});
            skLineSegment(sketch, "E420", {"start": v(-17.63, -18.37) * mm, "end": v(-17.5, -18.29) * mm});
            skLineSegment(sketch, "E421", {"start": v(-17.5, -18.29) * mm, "end": v(-17.4, -18.2) * mm});
            skLineSegment(sketch, "E422", {"start": v(-17.4, -18.2) * mm, "end": v(-17.32, -18.14) * mm});
            skLineSegment(sketch, "E423", {"start": v(-17.32, -18.14) * mm, "end": v(-17.25, -18.09) * mm});
            skLineSegment(sketch, "E424", {"start": v(-17.25, -18.09) * mm, "end": v(-17.2, -18.05) * mm});
            skLineSegment(sketch, "E425", {"start": v(-17.2, -18.05) * mm, "end": v(-17.17, -18.02) * mm});
            skLineSegment(sketch, "E426", {"start": v(-17.17, -18.02) * mm, "end": v(-17.16, -18) * mm});
            skLineSegment(sketch, "E427", {"start": v(-17.16, -18) * mm, "end": v(-14.76, -15.48) * mm});
            skLineSegment(sketch, "E428", {"start": v(-14.76, -15.48) * mm, "end": v(-10.7, -18.52) * mm});
            skLineSegment(sketch, "E429", {"start": v(-10.7, -18.52) * mm, "end": v(-12.43, -21.53) * mm});
            skLineSegment(sketch, "E430", {"start": v(-12.43, -21.53) * mm, "end": v(-12.44, -21.56) * mm});
            skLineSegment(sketch, "E431", {"start": v(-12.44, -21.56) * mm, "end": v(-12.46, -21.6) * mm});
            skLineSegment(sketch, "E432", {"start": v(-12.46, -21.6) * mm, "end": v(-12.5, -21.65) * mm});
            skLineSegment(sketch, "E433", {"start": v(-12.5, -21.65) * mm, "end": v(-12.52, -21.73) * mm});
            skLineSegment(sketch, "E434", {"start": v(-12.52, -21.73) * mm, "end": v(-12.56, -21.83) * mm});
            skLineSegment(sketch, "E435", {"start": v(-12.56, -21.83) * mm, "end": v(-12.6, -21.95) * mm});
            skLineSegment(sketch, "E436", {"start": v(-12.6, -21.95) * mm, "end": v(-12.65, -22.1) * mm});
            skLineSegment(sketch, "E437", {"start": v(-12.65, -22.1) * mm, "end": v(-12.7, -22.26) * mm});
            skLineSegment(sketch, "E438", {"start": v(-12.7, -22.26) * mm, "end": v(-12.75, -22.44) * mm});
            skLineSegment(sketch, "E439", {"start": v(-12.75, -22.44) * mm, "end": v(-12.8, -22.65) * mm});
            skLineSegment(sketch, "E440", {"start": v(-12.8, -22.65) * mm, "end": v(-12.85, -22.88) * mm});
            skLineSegment(sketch, "E441", {"start": v(-12.85, -22.88) * mm, "end": v(-12.9, -23.13) * mm});
            skLineSegment(sketch, "E442", {"start": v(-12.9, -23.13) * mm, "end": v(-12.93, -23.4) * mm});
            skLineSegment(sketch, "E443", {"start": v(-12.93, -23.4) * mm, "end": v(-12.96, -23.7) * mm});
            skLineSegment(sketch, "E444", {"start": v(-12.96, -23.7) * mm, "end": v(-12.99, -24.01) * mm});
            skLineSegment(sketch, "E445", {"start": v(-12.99, -24.01) * mm, "end": v(-13, -24.35) * mm});
            skLineSegment(sketch, "E446", {"start": v(-13, -24.35) * mm, "end": v(-13.02, -24.71) * mm});
            skLineSegment(sketch, "E447", {"start": v(-13.02, -24.71) * mm, "end": v(-13.02, -25.1) * mm});
            skLineSegment(sketch, "E448", {"start": v(-13.02, -25.1) * mm, "end": v(-13, -25.5) * mm});
            skLineSegment(sketch, "E449", {"start": v(-13, -25.5) * mm, "end": v(-12.98, -25.92) * mm});
            skLineSegment(sketch, "E450", {"start": v(-12.98, -25.92) * mm, "end": v(-12.94, -26.36) * mm});
            skLineSegment(sketch, "E451", {"start": v(-12.94, -26.36) * mm, "end": v(-12.88, -26.82) * mm});
            skLineSegment(sketch, "E452", {"start": v(-12.88, -26.82) * mm, "end": v(-12.81, -27.3) * mm});
            skLineSegment(sketch, "E453", {"start": v(-12.81, -27.3) * mm, "end": v(-12.72, -27.8) * mm});
            skLineSegment(sketch, "E454", {"start": v(-12.72, -27.8) * mm, "end": v(-12.56, -28.2) * mm});
            skLineSegment(sketch, "E455", {"start": v(-12.56, -28.2) * mm, "end": v(-10.36, -29.08) * mm});
            skLineSegment(sketch, "E456", {"start": v(-10.36, -29.08) * mm, "end": v(-9.97, -28.9) * mm});
            skLineSegment(sketch, "E457", {"start": v(-9.97, -28.9) * mm, "end": v(-9.56, -28.6) * mm});
            skLineSegment(sketch, "E458", {"start": v(-9.56, -28.6) * mm, "end": v(-9.18, -28.3) * mm});
            skLineSegment(sketch, "E459", {"start": v(-9.18, -28.3) * mm, "end": v(-8.82, -28) * mm});
            skLineSegment(sketch, "E460", {"start": v(-8.82, -28) * mm, "end": v(-8.49, -27.71) * mm});
            skLineSegment(sketch, "E461", {"start": v(-8.49, -27.71) * mm, "end": v(-8.18, -27.43) * mm});
            skLineSegment(sketch, "E462", {"start": v(-8.18, -27.43) * mm, "end": v(-7.9, -27.14) * mm});
            skLineSegment(sketch, "E463", {"start": v(-7.9, -27.14) * mm, "end": v(-7.63, -26.87) * mm});
            skLineSegment(sketch, "E464", {"start": v(-7.63, -26.87) * mm, "end": v(-7.39, -26.6) * mm});
            skLineSegment(sketch, "E465", {"start": v(-7.39, -26.6) * mm, "end": v(-7.17, -26.35) * mm});
            skLineSegment(sketch, "E466", {"start": v(-7.17, -26.35) * mm, "end": v(-6.97, -26.1) * mm});
            skLineSegment(sketch, "E467", {"start": v(-6.97, -26.1) * mm, "end": v(-6.79, -25.86) * mm});
            skLineSegment(sketch, "E468", {"start": v(-6.79, -25.86) * mm, "end": v(-6.63, -25.64) * mm});
            skLineSegment(sketch, "E469", {"start": v(-6.63, -25.64) * mm, "end": v(-6.49, -25.43) * mm});
            skLineSegment(sketch, "E470", {"start": v(-6.49, -25.43) * mm, "end": v(-6.36, -25.23) * mm});
            skLineSegment(sketch, "E471", {"start": v(-6.36, -25.23) * mm, "end": v(-6.25, -25.04) * mm});
            skLineSegment(sketch, "E472", {"start": v(-6.25, -25.04) * mm, "end": v(-6.16, -24.88) * mm});
            skLineSegment(sketch, "E473", {"start": v(-6.16, -24.88) * mm, "end": v(-6.09, -24.72) * mm});
            skLineSegment(sketch, "E474", {"start": v(-6.09, -24.72) * mm, "end": v(-6.02, -24.6) * mm});
            skLineSegment(sketch, "E475", {"start": v(-6.02, -24.6) * mm, "end": v(-5.97, -24.47) * mm});
            skLineSegment(sketch, "E476", {"start": v(-5.97, -24.47) * mm, "end": v(-5.93, -24.37) * mm});
            skLineSegment(sketch, "E477", {"start": v(-5.93, -24.37) * mm, "end": v(-5.9, -24.3) * mm});
            skLineSegment(sketch, "E478", {"start": v(-5.9, -24.3) * mm, "end": v(-5.88, -24.23) * mm});
            skLineSegment(sketch, "E479", {"start": v(-5.88, -24.23) * mm, "end": v(-5.86, -24.19) * mm});
            skLineSegment(sketch, "E480", {"start": v(-5.86, -24.19) * mm, "end": v(-5.86, -24.17) * mm});
            skLineSegment(sketch, "E481", {"start": v(-5.86, -24.17) * mm, "end": v(-5.04, -20.78) * mm});
            skLineSegment(sketch, "E482", {"start": v(-5.04, -20.78) * mm, "end": v(0, -21.39) * mm});
            skLineSegment(sketch, "E483", {"start": v(0, -21.39) * mm, "end": v(0, -24.87) * mm});
            skLineSegment(sketch, "E484", {"start": v(0, -24.87) * mm, "end": v(0, -24.9) * mm});
            skLineSegment(sketch, "E485", {"start": v(0, -24.9) * mm, "end": v(0, -24.93) * mm});
            skLineSegment(sketch, "E486", {"start": v(0, -24.93) * mm, "end": v(0, -25) * mm});
            skLineSegment(sketch, "E487", {"start": v(0, -25) * mm, "end": v(0.02, -25.08) * mm});
            skLineSegment(sketch, "E488", {"start": v(0.02, -25.08) * mm, "end": v(0.04, -25.2) * mm});
            skLineSegment(sketch, "E489", {"start": v(0.04, -25.2) * mm, "end": v(0.06, -25.32) * mm});
            skLineSegment(sketch, "E490", {"start": v(0.06, -25.32) * mm, "end": v(0.09, -25.46) * mm});
            skLineSegment(sketch, "E491", {"start": v(0.09, -25.46) * mm, "end": v(0.13, -25.63) * mm});
            skLineSegment(sketch, "E492", {"start": v(0.13, -25.63) * mm, "end": v(0.18, -25.81) * mm});
            skLineSegment(sketch, "E493", {"start": v(0.18, -25.81) * mm, "end": v(0.24, -26.02) * mm});
            skLineSegment(sketch, "E494", {"start": v(0.24, -26.02) * mm, "end": v(0.31, -26.24) * mm});
            skLineSegment(sketch, "E495", {"start": v(0.31, -26.24) * mm, "end": v(0.4, -26.48) * mm});
            skLineSegment(sketch, "E496", {"start": v(0.4, -26.48) * mm, "end": v(0.5, -26.73) * mm});
            skLineSegment(sketch, "E497", {"start": v(0.5, -26.73) * mm, "end": v(0.62, -27) * mm});
            skLineSegment(sketch, "E498", {"start": v(0.62, -27) * mm, "end": v(0.76, -27.3) * mm});
            skLineSegment(sketch, "E499", {"start": v(0.76, -27.3) * mm, "end": v(0.91, -27.6) * mm});
            skLineSegment(sketch, "E500", {"start": v(0.91, -27.6) * mm, "end": v(1.08, -27.91) * mm});
            skLineSegment(sketch, "E501", {"start": v(1.08, -27.91) * mm, "end": v(1.27, -28.24) * mm});
            skLineSegment(sketch, "E502", {"start": v(1.27, -28.24) * mm, "end": v(1.49, -28.58) * mm});
            skLineSegment(sketch, "E503", {"start": v(1.49, -28.58) * mm, "end": v(1.72, -28.93) * mm});
            skLineSegment(sketch, "E504", {"start": v(1.72, -28.93) * mm, "end": v(1.98, -29.3) * mm});
            skLineSegment(sketch, "E505", {"start": v(1.98, -29.3) * mm, "end": v(2.25, -29.67) * mm});
            skLineSegment(sketch, "E506", {"start": v(2.25, -29.67) * mm, "end": v(2.56, -30.05) * mm});
            skLineSegment(sketch, "E507", {"start": v(2.56, -30.05) * mm, "end": v(2.88, -30.44) * mm});
            skLineSegment(sketch, "E508", {"start": v(2.88, -30.44) * mm, "end": v(3.22, -30.7) * mm});
            skLineSegment(sketch, "E509", {"start": v(3.22, -30.7) * mm, "end": v(5.56, -30.36) * mm});
            skLineSegment(sketch, "E510", {"start": v(5.56, -30.36) * mm, "end": v(5.81, -30.01) * mm});
            skLineSegment(sketch, "E511", {"start": v(5.81, -30.01) * mm, "end": v(6.02, -29.55) * mm});
            skLineSegment(sketch, "E512", {"start": v(6.02, -29.55) * mm, "end": v(6.2, -29.1) * mm});
            skLineSegment(sketch, "E513", {"start": v(6.2, -29.1) * mm, "end": v(6.36, -28.66) * mm});
            skLineSegment(sketch, "E514", {"start": v(6.36, -28.66) * mm, "end": v(6.5, -28.25) * mm});
            skLineSegment(sketch, "E515", {"start": v(6.5, -28.25) * mm, "end": v(6.63, -27.84) * mm});
            skLineSegment(sketch, "E516", {"start": v(6.63, -27.84) * mm, "end": v(6.74, -27.45) * mm});
            skLineSegment(sketch, "E517", {"start": v(6.74, -27.45) * mm, "end": v(6.83, -27.08) * mm});
            skLineSegment(sketch, "E518", {"start": v(6.83, -27.08) * mm, "end": v(6.9, -26.73) * mm});
            skLineSegment(sketch, "E519", {"start": v(6.9, -26.73) * mm, "end": v(6.97, -26.4) * mm});
            skLineSegment(sketch, "E520", {"start": v(6.97, -26.4) * mm, "end": v(7.02, -26.08) * mm});
            skLineSegment(sketch, "E521", {"start": v(7.02, -26.08) * mm, "end": v(7.05, -25.8) * mm});
            skLineSegment(sketch, "E522", {"start": v(7.05, -25.8) * mm, "end": v(7.08, -25.52) * mm});
            skLineSegment(sketch, "E523", {"start": v(7.08, -25.52) * mm, "end": v(7.1, -25.26) * mm});
            skLineSegment(sketch, "E524", {"start": v(7.1, -25.26) * mm, "end": v(7.1, -25.03) * mm});
            skLineSegment(sketch, "E525", {"start": v(7.1, -25.03) * mm, "end": v(7.1, -24.82) * mm});
            skLineSegment(sketch, "E526", {"start": v(7.1, -24.82) * mm, "end": v(7.1, -24.63) * mm});
            skLineSegment(sketch, "E527", {"start": v(7.1, -24.63) * mm, "end": v(7.1, -24.45) * mm});
            skLineSegment(sketch, "E528", {"start": v(7.1, -24.45) * mm, "end": v(7.08, -24.3) * mm});
            skLineSegment(sketch, "E529", {"start": v(7.08, -24.3) * mm, "end": v(7.07, -24.18) * mm});
            skLineSegment(sketch, "E530", {"start": v(7.07, -24.18) * mm, "end": v(7.05, -24.07) * mm});
            skLineSegment(sketch, "E531", {"start": v(7.05, -24.07) * mm, "end": v(7.04, -23.99) * mm});
            skLineSegment(sketch, "E532", {"start": v(7.04, -23.99) * mm, "end": v(7.03, -23.92) * mm});
            skLineSegment(sketch, "E533", {"start": v(7.03, -23.92) * mm, "end": v(7.02, -23.88) * mm});
            skLineSegment(sketch, "E534", {"start": v(7.02, -23.88) * mm, "end": v(7.01, -23.86) * mm});
            skLineSegment(sketch, "E535", {"start": v(7.01, -23.86) * mm, "end": v(6.03, -20.52) * mm});
            skLineSegment(sketch, "E536", {"start": v(6.03, -20.52) * mm, "end": v(10.7, -18.52) * mm});
            skLineSegment(sketch, "E537", {"start": v(10.7, -18.52) * mm, "end": v(12.43, -21.53) * mm});
            skLineSegment(sketch, "E538", {"start": v(12.43, -21.53) * mm, "end": v(12.45, -21.56) * mm});
            skLineSegment(sketch, "E539", {"start": v(12.45, -21.56) * mm, "end": v(12.5, -21.64) * mm});
            skLineSegment(sketch, "E540", {"start": v(12.5, -21.64) * mm, "end": v(12.56, -21.71) * mm});
            skLineSegment(sketch, "E541", {"start": v(12.56, -21.71) * mm, "end": v(12.63, -21.8) * mm});
            skLineSegment(sketch, "E542", {"start": v(12.63, -21.8) * mm, "end": v(12.7, -21.9) * mm});
            skLineSegment(sketch, "E543", {"start": v(12.7, -21.9) * mm, "end": v(12.8, -22) * mm});
            skLineSegment(sketch, "E544", {"start": v(12.8, -22) * mm, "end": v(12.93, -22.13) * mm});
            skLineSegment(sketch, "E545", {"start": v(12.93, -22.13) * mm, "end": v(13.06, -22.26) * mm});
            skLineSegment(sketch, "E546", {"start": v(13.06, -22.26) * mm, "end": v(13.22, -22.41) * mm});
            skLineSegment(sketch, "E547", {"start": v(13.22, -22.41) * mm, "end": v(13.4, -22.57) * mm});
            skLineSegment(sketch, "E548", {"start": v(13.4, -22.57) * mm, "end": v(13.59, -22.73) * mm});
            skLineSegment(sketch, "E549", {"start": v(13.59, -22.73) * mm, "end": v(13.8, -22.9) * mm});
            skLineSegment(sketch, "E550", {"start": v(13.8, -22.9) * mm, "end": v(14.04, -23.08) * mm});
            skLineSegment(sketch, "E551", {"start": v(14.04, -23.08) * mm, "end": v(14.3, -23.26) * mm});
            skLineSegment(sketch, "E552", {"start": v(14.3, -23.26) * mm, "end": v(14.59, -23.44) * mm});
            skLineSegment(sketch, "E553", {"start": v(14.59, -23.44) * mm, "end": v(14.9, -23.63) * mm});
            skLineSegment(sketch, "E554", {"start": v(14.9, -23.63) * mm, "end": v(15.22, -23.82) * mm});
            skLineSegment(sketch, "E555", {"start": v(15.22, -23.82) * mm, "end": v(15.58, -24) * mm});
            skLineSegment(sketch, "E556", {"start": v(15.58, -24) * mm, "end": v(15.96, -24.2) * mm});
            skLineSegment(sketch, "E557", {"start": v(15.96, -24.2) * mm, "end": v(16.36, -24.38) * mm});
            skLineSegment(sketch, "E558", {"start": v(16.36, -24.38) * mm, "end": v(16.79, -24.57) * mm});
            skLineSegment(sketch, "E559", {"start": v(16.79, -24.57) * mm, "end": v(17.24, -24.74) * mm});
            skLineSegment(sketch, "E560", {"start": v(17.24, -24.74) * mm, "end": v(17.72, -24.92) * mm});
            skLineSegment(sketch, "E561", {"start": v(17.72, -24.92) * mm, "end": v(18.14, -24.98) * mm});
            skLineSegment(sketch, "E562", {"start": v(18.14, -24.98) * mm, "end": v(20, -23.51) * mm});
            skLineSegment(sketch, "E563", {"start": v(20, -23.51) * mm, "end": v(20.04, -23.09) * mm});
            skLineSegment(sketch, "E564", {"start": v(20.04, -23.09) * mm, "end": v(19.99, -22.58) * mm});
            skLineSegment(sketch, "E565", {"start": v(19.99, -22.58) * mm, "end": v(19.92, -22.1) * mm});
            skLineSegment(sketch, "E566", {"start": v(19.92, -22.1) * mm, "end": v(19.84, -21.64) * mm});
            skLineSegment(sketch, "E567", {"start": v(19.84, -21.64) * mm, "end": v(19.76, -21.2) * mm});
            skLineSegment(sketch, "E568", {"start": v(19.76, -21.2) * mm, "end": v(19.66, -20.8) * mm});
            skLineSegment(sketch, "E569", {"start": v(19.66, -20.8) * mm, "end": v(19.56, -20.4) * mm});
            skLineSegment(sketch, "E570", {"start": v(19.56, -20.4) * mm, "end": v(19.46, -20.04) * mm});
            skLineSegment(sketch, "E571", {"start": v(19.46, -20.04) * mm, "end": v(19.35, -19.7) * mm});
            skLineSegment(sketch, "E572", {"start": v(19.35, -19.7) * mm, "end": v(19.23, -19.38) * mm});
            skLineSegment(sketch, "E573", {"start": v(19.23, -19.38) * mm, "end": v(19.12, -19.08) * mm});
            skLineSegment(sketch, "E574", {"start": v(19.12, -19.08) * mm, "end": v(19, -18.81) * mm});
            skLineSegment(sketch, "E575", {"start": v(19, -18.81) * mm, "end": v(18.89, -18.56) * mm});
            skLineSegment(sketch, "E576", {"start": v(18.89, -18.56) * mm, "end": v(18.78, -18.33) * mm});
            skLineSegment(sketch, "E577", {"start": v(18.78, -18.33) * mm, "end": v(18.67, -18.12) * mm});
            skLineSegment(sketch, "E578", {"start": v(18.67, -18.12) * mm, "end": v(18.56, -17.94) * mm});
            skLineSegment(sketch, "E579", {"start": v(18.56, -17.94) * mm, "end": v(18.46, -17.78) * mm});
            skLineSegment(sketch, "E580", {"start": v(18.46, -17.78) * mm, "end": v(18.37, -17.63) * mm});
            skLineSegment(sketch, "E581", {"start": v(18.37, -17.63) * mm, "end": v(18.29, -17.5) * mm});
            skLineSegment(sketch, "E582", {"start": v(18.29, -17.5) * mm, "end": v(18.2, -17.4) * mm});
            skLineSegment(sketch, "E583", {"start": v(18.2, -17.4) * mm, "end": v(18.14, -17.32) * mm});
            skLineSegment(sketch, "E584", {"start": v(18.14, -17.32) * mm, "end": v(18.09, -17.25) * mm});
            skLineSegment(sketch, "E585", {"start": v(18.09, -17.25) * mm, "end": v(18.05, -17.2) * mm});
            skLineSegment(sketch, "E586", {"start": v(18.05, -17.2) * mm, "end": v(18.02, -17.17) * mm});
            skLineSegment(sketch, "E587", {"start": v(18.02, -17.17) * mm, "end": v(18, -17.16) * mm});
            skLineSegment(sketch, "E588", {"start": v(18, -17.16) * mm, "end": v(15.48, -14.76) * mm});
            skLineSegment(sketch, "E589", {"start": v(15.48, -14.76) * mm, "end": v(18.52, -10.7) * mm});
            skLineSegment(sketch, "E590", {"start": v(18.52, -10.7) * mm, "end": v(21.53, -12.43) * mm});
            skLineSegment(sketch, "E591", {"start": v(21.53, -12.43) * mm, "end": v(21.56, -12.44) * mm});
            skLineSegment(sketch, "E592", {"start": v(21.56, -12.44) * mm, "end": v(21.6, -12.46) * mm});
            skLineSegment(sketch, "E593", {"start": v(21.6, -12.46) * mm, "end": v(21.65, -12.5) * mm});
            skLineSegment(sketch, "E594", {"start": v(21.65, -12.5) * mm, "end": v(21.73, -12.52) * mm});
            skLineSegment(sketch, "E595", {"start": v(21.73, -12.52) * mm, "end": v(21.83, -12.56) * mm});
            skLineSegment(sketch, "E596", {"start": v(21.83, -12.56) * mm, "end": v(21.95, -12.6) * mm});
            skLineSegment(sketch, "E597", {"start": v(21.95, -12.6) * mm, "end": v(22.1, -12.65) * mm});
            skLineSegment(sketch, "E598", {"start": v(22.1, -12.65) * mm, "end": v(22.26, -12.7) * mm});
            skLineSegment(sketch, "E599", {"start": v(22.26, -12.7) * mm, "end": v(22.44, -12.75) * mm});
            skLineSegment(sketch, "E600", {"start": v(22.44, -12.75) * mm, "end": v(22.65, -12.8) * mm});
            skLineSegment(sketch, "E601", {"start": v(22.65, -12.8) * mm, "end": v(22.88, -12.85) * mm});
            skLineSegment(sketch, "E602", {"start": v(22.88, -12.85) * mm, "end": v(23.13, -12.9) * mm});
            skLineSegment(sketch, "E603", {"start": v(23.13, -12.9) * mm, "end": v(23.4, -12.93) * mm});
            skLineSegment(sketch, "E604", {"start": v(23.4, -12.93) * mm, "end": v(23.7, -12.96) * mm});
            skLineSegment(sketch, "E605", {"start": v(23.7, -12.96) * mm, "end": v(24.02, -12.99) * mm});
            skLineSegment(sketch, "E606", {"start": v(24.02, -12.99) * mm, "end": v(24.35, -13) * mm});
            skLineSegment(sketch, "E607", {"start": v(24.35, -13) * mm, "end": v(24.71, -13.02) * mm});
            skLineSegment(sketch, "E608", {"start": v(24.71, -13.02) * mm, "end": v(25.1, -13.02) * mm});
            skLineSegment(sketch, "E609", {"start": v(25.1, -13.02) * mm, "end": v(25.5, -13) * mm});
            skLineSegment(sketch, "E610", {"start": v(25.5, -13) * mm, "end": v(25.92, -12.98) * mm});
            skLineSegment(sketch, "E611", {"start": v(25.92, -12.98) * mm, "end": v(26.36, -12.94) * mm});
            skLineSegment(sketch, "E612", {"start": v(26.36, -12.94) * mm, "end": v(26.82, -12.88) * mm});
            skLineSegment(sketch, "E613", {"start": v(26.82, -12.88) * mm, "end": v(27.3, -12.81) * mm});
            skLineSegment(sketch, "E614", {"start": v(27.3, -12.81) * mm, "end": v(27.8, -12.72) * mm});
            skLineSegment(sketch, "E615", {"start": v(27.8, -12.72) * mm, "end": v(28.2, -12.56) * mm});
            skLineSegment(sketch, "E616", {"start": v(28.2, -12.56) * mm, "end": v(29.08, -10.36) * mm});
            skLineSegment(sketch, "E617", {"start": v(29.08, -10.36) * mm, "end": v(28.9, -9.97) * mm});
            skLineSegment(sketch, "E618", {"start": v(28.9, -9.97) * mm, "end": v(28.6, -9.56) * mm});
            skLineSegment(sketch, "E619", {"start": v(28.6, -9.56) * mm, "end": v(28.3, -9.18) * mm});
            skLineSegment(sketch, "E620", {"start": v(28.3, -9.18) * mm, "end": v(28, -8.82) * mm});
            skLineSegment(sketch, "E621", {"start": v(28, -8.82) * mm, "end": v(27.71, -8.49) * mm});
            skLineSegment(sketch, "E622", {"start": v(27.71, -8.49) * mm, "end": v(27.43, -8.18) * mm});
            skLineSegment(sketch, "E623", {"start": v(27.43, -8.18) * mm, "end": v(27.14, -7.9) * mm});
            skLineSegment(sketch, "E624", {"start": v(27.14, -7.9) * mm, "end": v(26.87, -7.63) * mm});
            skLineSegment(sketch, "E625", {"start": v(26.87, -7.63) * mm, "end": v(26.6, -7.39) * mm});
            skLineSegment(sketch, "E626", {"start": v(26.6, -7.39) * mm, "end": v(26.35, -7.17) * mm});
            skLineSegment(sketch, "E627", {"start": v(26.35, -7.17) * mm, "end": v(26.1, -6.97) * mm});
            skLineSegment(sketch, "E628", {"start": v(26.1, -6.97) * mm, "end": v(25.86, -6.79) * mm});
            skLineSegment(sketch, "E629", {"start": v(25.86, -6.79) * mm, "end": v(25.64, -6.63) * mm});
            skLineSegment(sketch, "E630", {"start": v(25.64, -6.63) * mm, "end": v(25.43, -6.49) * mm});
            skLineSegment(sketch, "E631", {"start": v(25.43, -6.49) * mm, "end": v(25.23, -6.36) * mm});
            skLineSegment(sketch, "E632", {"start": v(25.23, -6.36) * mm, "end": v(25.04, -6.25) * mm});
            skLineSegment(sketch, "E633", {"start": v(25.04, -6.25) * mm, "end": v(24.88, -6.16) * mm});
            skLineSegment(sketch, "E634", {"start": v(24.88, -6.16) * mm, "end": v(24.72, -6.09) * mm});
            skLineSegment(sketch, "E635", {"start": v(24.72, -6.09) * mm, "end": v(24.6, -6.02) * mm});
            skLineSegment(sketch, "E636", {"start": v(24.6, -6.02) * mm, "end": v(24.47, -5.97) * mm});
            skLineSegment(sketch, "E637", {"start": v(24.47, -5.97) * mm, "end": v(24.37, -5.93) * mm});
            skLineSegment(sketch, "E638", {"start": v(24.37, -5.93) * mm, "end": v(24.3, -5.9) * mm});
            skLineSegment(sketch, "E639", {"start": v(24.3, -5.9) * mm, "end": v(24.23, -5.88) * mm});
            skLineSegment(sketch, "E640", {"start": v(24.23, -5.88) * mm, "end": v(24.19, -5.86) * mm});
            skLineSegment(sketch, "E641", {"start": v(24.19, -5.86) * mm, "end": v(24.17, -5.86) * mm});
            skLineSegment(sketch, "E642", {"start": v(24.17, -5.86) * mm, "end": v(20.79, -5.04) * mm});
            skLineSegment(sketch, "E643", {"start": v(20.79, -5.04) * mm, "end": v(21.39, 0) * mm});
            skSolve(sketch);
        }
        {
            var Q0;
            Q0=makeQuery(id+"F0.imprint","IMPRINT",FACE,{"disambiguationData":[TD([[makeQuery(id+"F0.imprint","IMPRINT",EDGE,{"derivedFrom":sQuery(id+"F0.wireOp",EDGE,"E0")}),1.0]])]});
            extrude(context, id + "F1", {"entities" : qUnion([Q0]), "depth" : 6.35 * mm});
        }
    });
